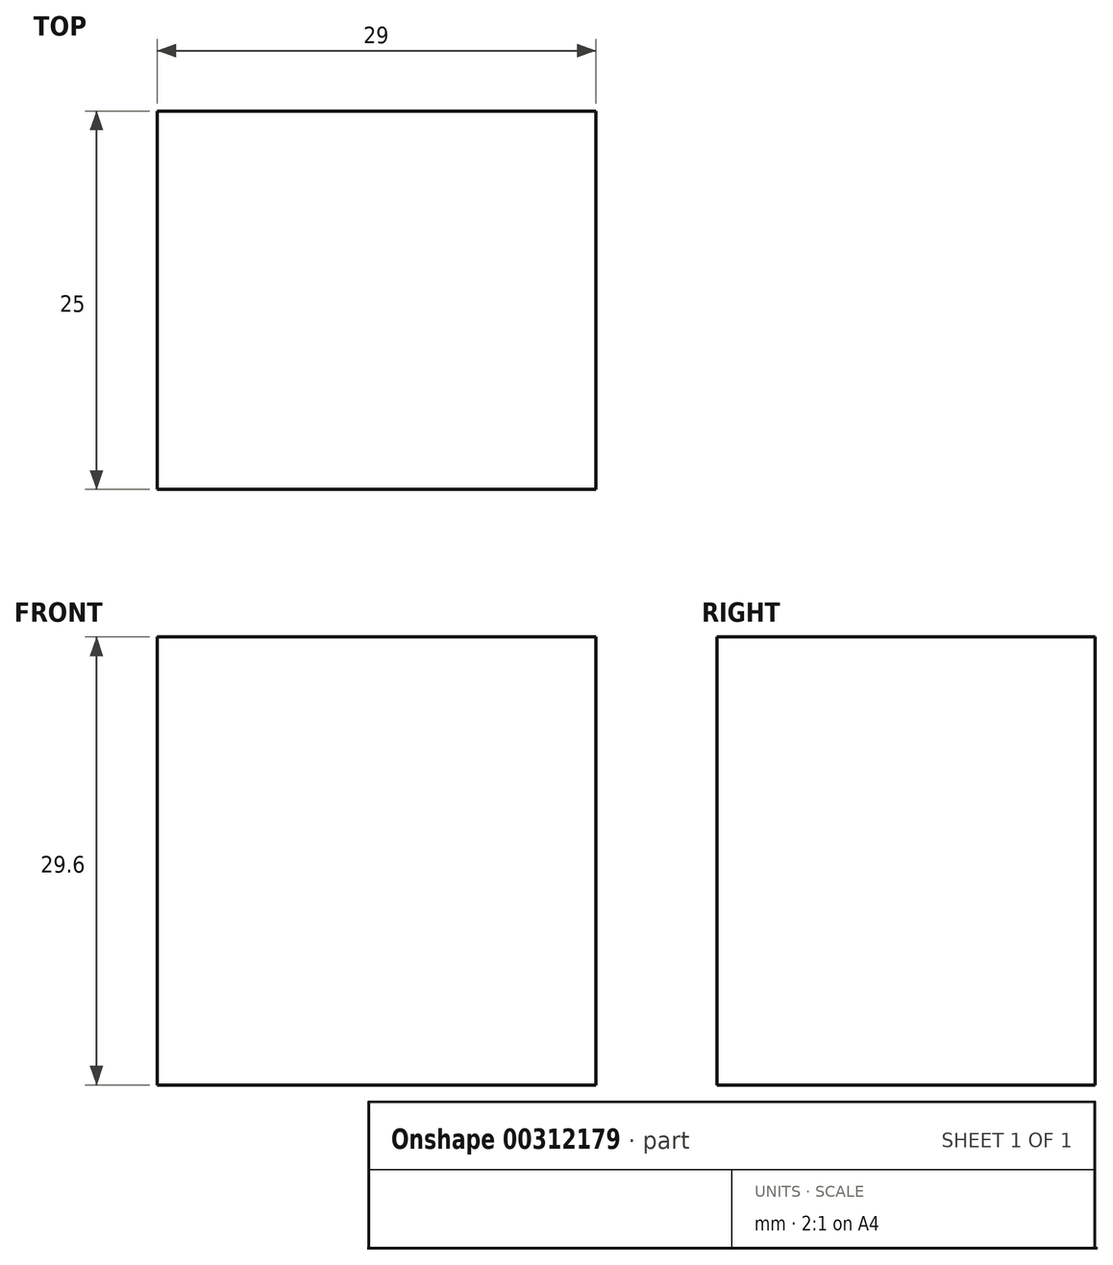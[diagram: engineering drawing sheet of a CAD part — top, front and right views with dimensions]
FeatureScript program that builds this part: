
annotation { "Feature Type Name" : "Feature", "Feature Type Description" : "" }
export const myFeature = defineFeature(function(context is Context, id is Id, definition is map)
    precondition{}
    {
        {
            var Q0;
            Q0=qCreatedBy(makeId("Front.planeOp"),FACE);
            var sketch = newSketch(context, id + "F0", { "sketchPlane" : qUnion([Q0])});
            skLineSegment(sketch, "E0.bottom", {"start": v(-13.68, 14.8) * mm, "end": v(15.32, 14.8) * mm});
            skLineSegment(sketch, "E0.top", {"start": v(-13.68, -14.8) * mm, "end": v(15.32, -14.8) * mm});
            skLineSegment(sketch, "E0.left", {"start": v(-13.68, 14.8) * mm, "end": v(-13.68, -14.8) * mm});
            skLineSegment(sketch, "E0.right", {"start": v(15.32, 14.8) * mm, "end": v(15.32, -14.8) * mm});
            skPoint(sketch, "E0.middle", {"position": v(0.82, 0) * mm});
            skSolve(sketch);
        }
        {
            var Q0;
            Q0 = qSketchRegion(id + "F0", true);
            extrude(context, id + "F1", {"entities" : qUnion([Q0]), "depth" : 25 * mm});
        }
    });
